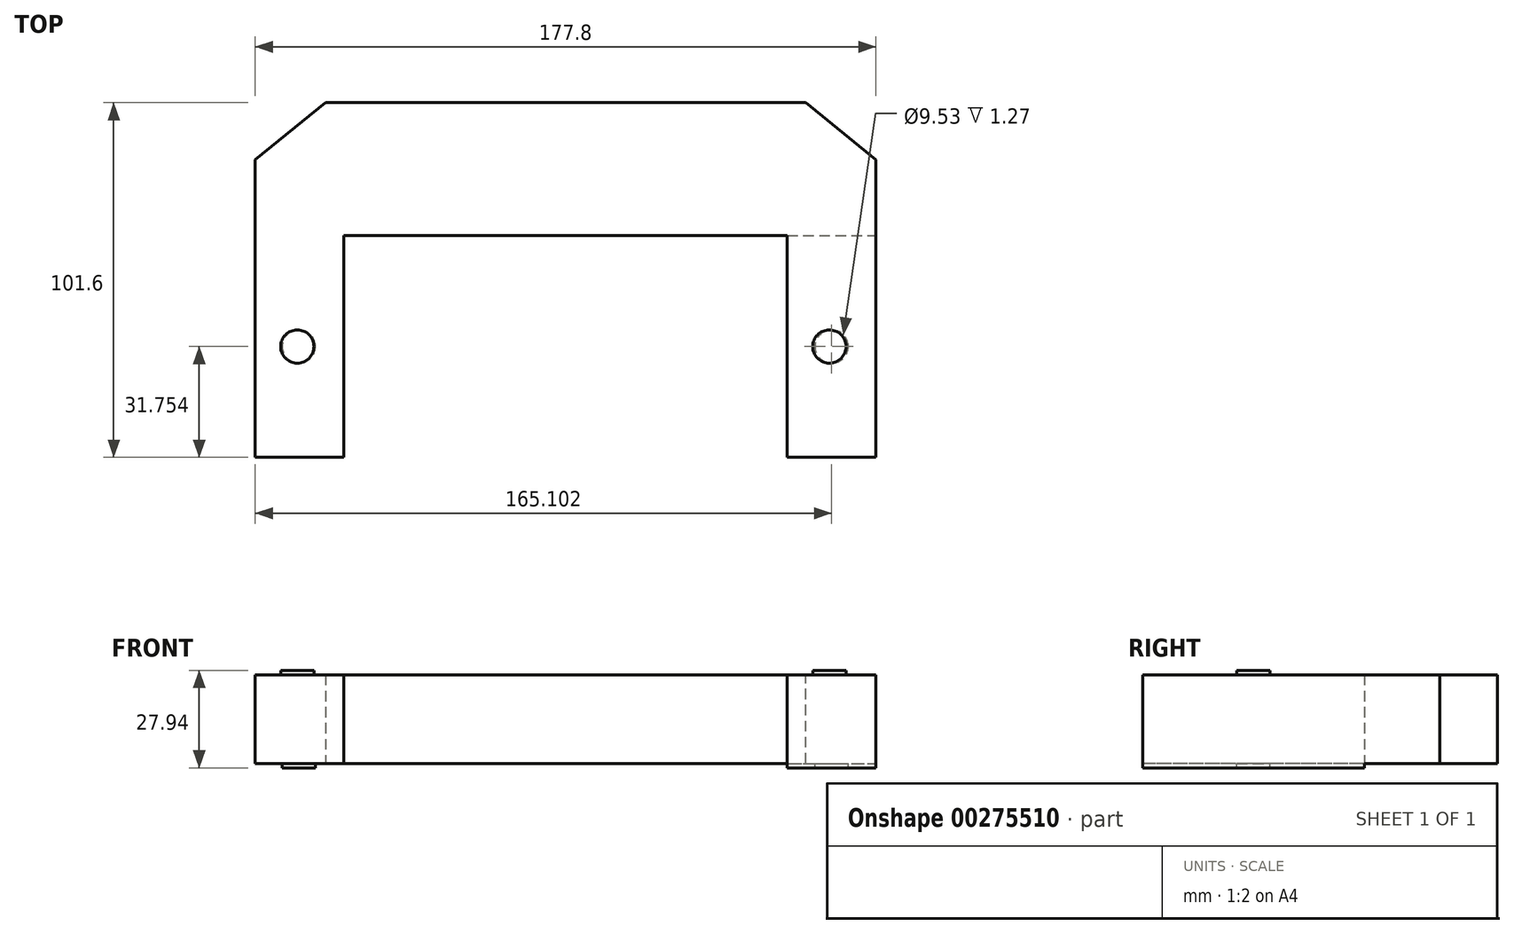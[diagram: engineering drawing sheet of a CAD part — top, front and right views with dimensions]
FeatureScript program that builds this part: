
annotation { "Feature Type Name" : "Feature", "Feature Type Description" : "" }
export const myFeature = defineFeature(function(context is Context, id is Id, definition is map)
    precondition{}
    {
        {
            var Q0;
            Q0=qCreatedBy(makeId("Top.planeOp"),FACE);
            var sketch = newSketch(context, id + "F0", { "sketchPlane" : qUnion([Q0])});
            skLineSegment(sketch, "E0.bottom", {"start": v(-82.57, 52.67) * mm, "end": v(95.23, 52.67) * mm});
            skLineSegment(sketch, "E0.top", {"start": v(-82.57, 14.57) * mm, "end": v(95.23, 14.57) * mm});
            skLineSegment(sketch, "E0.left", {"start": v(-82.57, 52.67) * mm, "end": v(-82.57, 14.57) * mm});
            skLineSegment(sketch, "E0.right", {"start": v(95.23, 52.67) * mm, "end": v(95.23, 14.57) * mm});
            skPoint(sketch, "E1.visualSharp", {"position": v(-82.57, 52.67) * mm});
            skLineSegment(sketch, "E1.filletArc", {"start": v(-82.57, 52.67) * mm, "end": v(-82.57, 52.67) * mm});
            skPoint(sketch, "E2.visualSharp", {"position": v(95.23, 52.67) * mm});
            skLineSegment(sketch, "E2.filletArc", {"start": v(95.23, 52.67) * mm, "end": v(95.23, 52.67) * mm});
            skLineSegment(sketch, "E3.bottom", {"start": v(-82.57, 14.57) * mm, "end": v(-57.17, 14.57) * mm});
            skLineSegment(sketch, "E3.top", {"start": v(-82.57, -48.93) * mm, "end": v(-57.17, -48.93) * mm});
            skLineSegment(sketch, "E3.left", {"start": v(-82.57, 14.57) * mm, "end": v(-82.57, -48.93) * mm});
            skLineSegment(sketch, "E3.right", {"start": v(-57.17, 14.57) * mm, "end": v(-57.17, -48.93) * mm});
            skLineSegment(sketch, "E4.bottom", {"start": v(95.23, 14.57) * mm, "end": v(69.83, 14.57) * mm});
            skLineSegment(sketch, "E4.top", {"start": v(95.23, -48.93) * mm, "end": v(69.83, -48.93) * mm});
            skLineSegment(sketch, "E4.left", {"start": v(95.23, 14.57) * mm, "end": v(95.23, -48.93) * mm});
            skLineSegment(sketch, "E4.right", {"start": v(69.83, 14.57) * mm, "end": v(69.83, -48.93) * mm});
            skSolve(sketch);
        }
        {
            var Q0;
            Q0 = qSketchRegion(id + "F0", true);
            extrude(context, id + "F1", {"entities" : qUnion([Q0]), "depth" : 25.4 * mm});
        }
        {
            var Q0;
            Q0=makeQuery(id+"F1.opExtrude","CAP_FACE",FACE,{"disambiguationData":[OSD([sQuery(id+"F0.wireOp",EDGE,"E0.bottom"),sQuery(id+"F0.wireOp",EDGE,"E0.top"),sQuery(id+"F0.wireOp",EDGE,"E0.left"),sQuery(id+"F0.wireOp",EDGE,"E0.right"),sQuery(id+"F0.wireOp",EDGE,"E3.top"),sQuery(id+"F0.wireOp",EDGE,"E3.left"),sQuery(id+"F0.wireOp",EDGE,"E3.right"),sQuery(id+"F0.wireOp",EDGE,"E4.top"),sQuery(id+"F0.wireOp",EDGE,"E4.left"),sQuery(id+"F0.wireOp",EDGE,"E4.right")])],"isStart":false});
            var sketch = newSketch(context, id + "F2", { "sketchPlane" : qUnion([Q0])});
            skLineSegment(sketch, "E5", {"start": v(-99.05, 22.97) * mm, "end": v(-44.52, 67.16) * mm});
            skLineSegment(sketch, "E6", {"start": v(-44.52, 67.16) * mm, "end": v(-66.75, 76.2) * mm});
            skLineSegment(sketch, "E7", {"start": v(-66.75, 76.2) * mm, "end": v(-104.48, 40.28) * mm});
            skLineSegment(sketch, "E8", {"start": v(-104.48, 40.28) * mm, "end": v(-99.05, 22.97) * mm});
            skLineSegment(sketch, "E9", {"start": v(63.53, 62.17) * mm, "end": v(115.33, 19.86) * mm});
            skLineSegment(sketch, "E10", {"start": v(115.33, 19.86) * mm, "end": v(133.18, 37.42) * mm});
            skLineSegment(sketch, "E11", {"start": v(133.18, 37.42) * mm, "end": v(81.95, 70.51) * mm});
            skLineSegment(sketch, "E12", {"start": v(81.95, 70.51) * mm, "end": v(63.53, 62.17) * mm});
            skSolve(sketch);
        }
        {
            var Q0;
            Q0 = qSketchRegion(id + "F2", true);
            extrude(context, id + "F3", {"entities" : qUnion([Q0]), "operationType" : NewBodyOperationType.REMOVE, "oppositeDirection" : true, "depth" : 25.4 * mm});
        }
        {
            var Q0;
            Q0=makeQuery(id+"F1.opExtrude","CAP_FACE",FACE,{"disambiguationData":[OSD([sQuery(id+"F0.wireOp",EDGE,"E0.bottom"),sQuery(id+"F0.wireOp",EDGE,"E0.top"),sQuery(id+"F0.wireOp",EDGE,"E0.left"),sQuery(id+"F0.wireOp",EDGE,"E0.right"),sQuery(id+"F0.wireOp",EDGE,"E3.top"),sQuery(id+"F0.wireOp",EDGE,"E3.left"),sQuery(id+"F0.wireOp",EDGE,"E3.right"),sQuery(id+"F0.wireOp",EDGE,"E4.top"),sQuery(id+"F0.wireOp",EDGE,"E4.left"),sQuery(id+"F0.wireOp",EDGE,"E4.right")])],"isStart":false});
            var sketch = newSketch(context, id + "F4", { "sketchPlane" : qUnion([Q0])});
            skCircle(sketch, "E13", {"center": v(-70.51, -17.18) * mm, "radius": 4.76 * mm});
            skLineSegment(sketch, "E14", {"start": v(-57.17, 14.57) * mm, "end": v(-82.57, 14.57) * mm});
            skLineSegment(sketch, "E15", {"start": v(-82.57, 14.57) * mm, "end": v(95.23, 14.57) * mm});
            skCircle(sketch, "E16", {"center": v(81.9, -17.18) * mm, "radius": 4.76 * mm});
            skSolve(sketch);
        }
        {
            var Q0;
            Q0=makeQuery(id+"F4.imprint","IMPRINT",FACE,{"disambiguationData":[TD([[makeQuery(id+"F4.imprint","IMPRINT",EDGE,{"derivedFrom":sQuery(id+"F4.wireOp",EDGE,"E13")}),1.0]])]});
            var Q1;
            Q1=makeQuery(id+"F4.imprint","IMPRINT",FACE,{"disambiguationData":[TD([[makeQuery(id+"F4.imprint","IMPRINT",EDGE,{"derivedFrom":sQuery(id+"F4.wireOp",EDGE,"E16")}),1.0]])]});
            extrude(context, id + "F5", {"entities" : qUnion([Q0, Q1]), "operationType" : NewBodyOperationType.ADD, "depth" : 1.27 * mm});
        }
        {
            var Q0;
            Q0=makeQuery(id+"F1.opExtrude","CAP_FACE",FACE,{"disambiguationData":[OSD([sQuery(id+"F0.wireOp",EDGE,"E0.bottom"),sQuery(id+"F0.wireOp",EDGE,"E0.top"),sQuery(id+"F0.wireOp",EDGE,"E0.left"),sQuery(id+"F0.wireOp",EDGE,"E0.right"),sQuery(id+"F0.wireOp",EDGE,"E3.top"),sQuery(id+"F0.wireOp",EDGE,"E3.left"),sQuery(id+"F0.wireOp",EDGE,"E3.right"),sQuery(id+"F0.wireOp",EDGE,"E4.top"),sQuery(id+"F0.wireOp",EDGE,"E4.left"),sQuery(id+"F0.wireOp",EDGE,"E4.right")])],"isStart":true});
            var sketch = newSketch(context, id + "F6", { "sketchPlane" : qUnion([Q0])});
            skCircle(sketch, "E17", {"center": v(-70.09, 17.18) * mm, "radius": 4.76 * mm});
            skLineSegment(sketch, "E18", {"start": v(69.83, -14.57) * mm, "end": v(-82.57, -14.57) * mm});
            skLineSegment(sketch, "E19", {"start": v(-82.57, -14.57) * mm, "end": v(95.23, -14.57) * mm});
            skLineSegment(sketch, "E20", {"start": v(82.53, 48.93) * mm, "end": v(82.53, -14.57) * mm});
            skCircle(sketch, "E21", {"center": v(82.53, 17.18) * mm, "radius": 4.76 * mm});
            skLineSegment(sketch, "E22", {"start": v(-70.09, 48.93) * mm, "end": v(-70.09, -14.57) * mm});
            skSolve(sketch);
        }
        {
            var Q0;
            {var subQ0=sQuery(id+"F6.wireOp",EDGE,"E21");var subQ1=sQuery(id+"F6.wireOp",EDGE,"E20");var subQ2=makeQuery(id+"F6.imprint","INTERSECT",VERTEX,{"disambiguationData":[OD(0.0)],"derivedFrom":[subQ1,subQ0]});Q0=makeQuery(id+"F6.imprint","IMPRINT",FACE,{"disambiguationData":[TD([[makeQuery(id+"F6.imprint","IMPRINT",EDGE,{"disambiguationData":[TD([[subQ2,-1.0]])],"derivedFrom":subQ1}),-1.0]])]});}
            var Q1;
            {var subQ0=sQuery(id+"F6.wireOp",EDGE,"E21");var subQ1=sQuery(id+"F6.wireOp",EDGE,"E20");var subQ2=makeQuery(id+"F6.imprint","INTERSECT",VERTEX,{"disambiguationData":[OD(0.0)],"derivedFrom":[subQ1,subQ0]});Q1=makeQuery(id+"F6.imprint","IMPRINT",FACE,{"disambiguationData":[TD([[makeQuery(id+"F6.imprint","IMPRINT",EDGE,{"disambiguationData":[TD([[subQ2,-1.0]])],"derivedFrom":subQ1}),1.0]])]});}
            var Q2;
            {var subQ0=sQuery(id+"F6.wireOp",EDGE,"E22");var subQ1=sQuery(id+"F6.wireOp",EDGE,"E17");var subQ2=makeQuery(id+"F6.imprint","INTERSECT",VERTEX,{"disambiguationData":[OD(0.0)],"derivedFrom":[subQ1,subQ0]});Q2=makeQuery(id+"F6.imprint","IMPRINT",FACE,{"disambiguationData":[TD([[makeQuery(id+"F6.imprint","IMPRINT",EDGE,{"disambiguationData":[TD([[subQ2,1.0]])],"derivedFrom":subQ1}),1.0]])]});}
            var Q3;
            {var subQ0=sQuery(id+"F6.wireOp",EDGE,"E22");var subQ1=sQuery(id+"F6.wireOp",EDGE,"E17");var subQ2=makeQuery(id+"F6.imprint","INTERSECT",VERTEX,{"disambiguationData":[OD(0.0)],"derivedFrom":[subQ1,subQ0]});Q3=makeQuery(id+"F6.imprint","IMPRINT",FACE,{"disambiguationData":[TD([[makeQuery(id+"F6.imprint","IMPRINT",EDGE,{"disambiguationData":[TD([[subQ2,-1.0]])],"derivedFrom":subQ1}),1.0]])]});}
            extrude(context, id + "F7", {"entities" : qUnion([Q0, Q1, Q2, Q3]), "operationType" : NewBodyOperationType.ADD, "depth" : 1.27 * mm});
        }
    });
